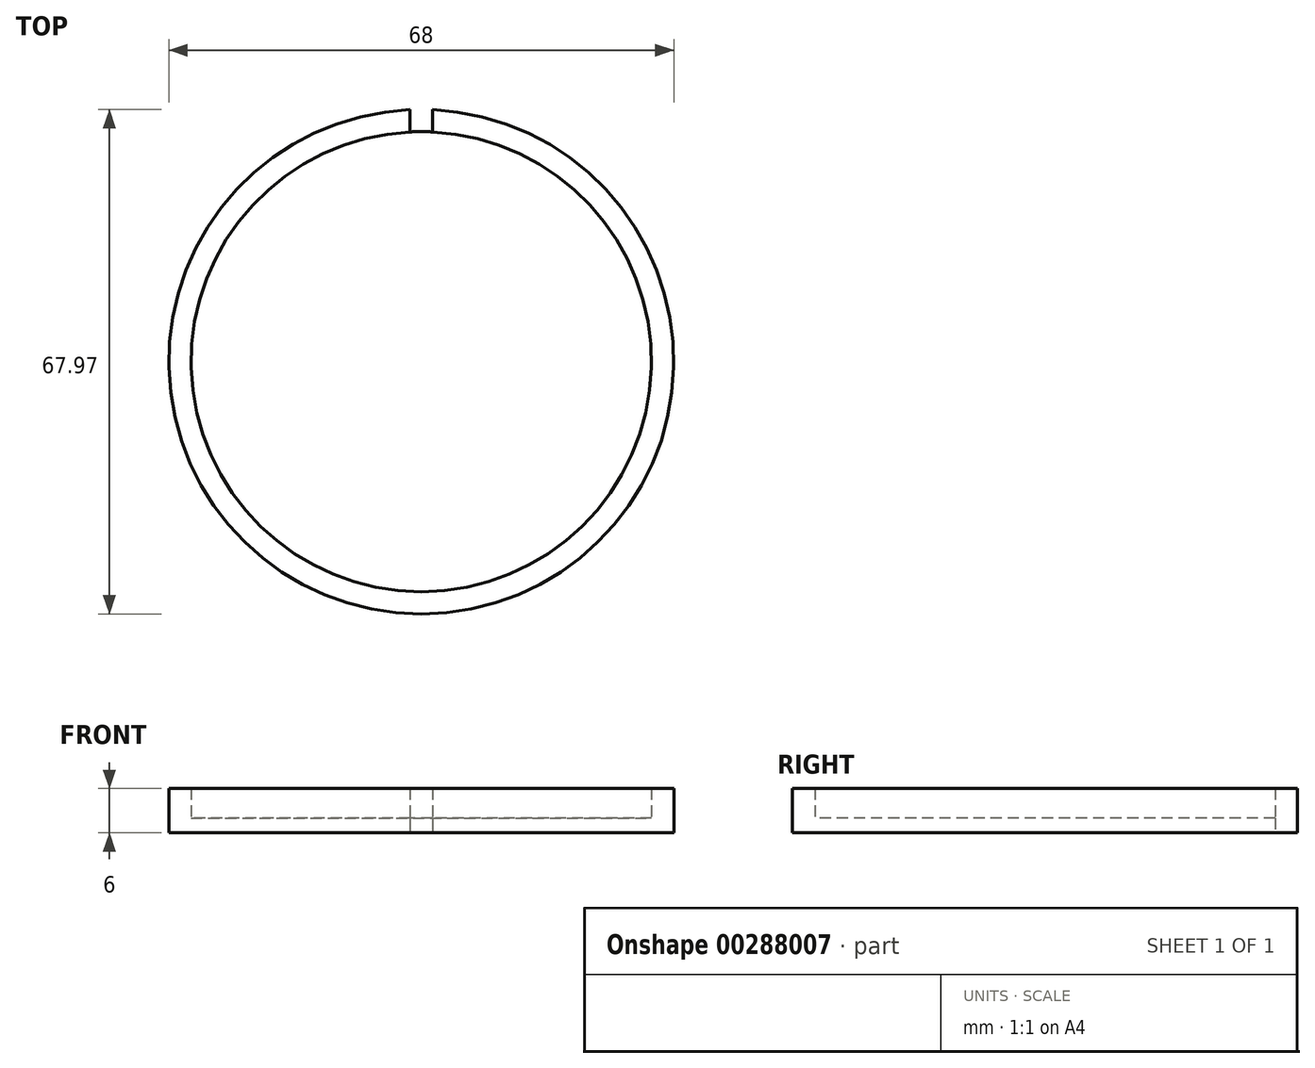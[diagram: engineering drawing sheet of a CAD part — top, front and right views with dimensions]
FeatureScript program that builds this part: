
annotation { "Feature Type Name" : "Feature", "Feature Type Description" : "" }
export const myFeature = defineFeature(function(context is Context, id is Id, definition is map)
    precondition{}
    {
        {
            var Q0;
            Q0=qCreatedBy(makeId("Top.planeOp"),FACE);
            var sketch = newSketch(context, id + "F0", { "sketchPlane" : qUnion([Q0])});
            skCircle(sketch, "E0", {"center": v(0, 0) * mm, "radius": 34 * mm});
            skCircle(sketch, "E1", {"center": v(0, 0) * mm, "radius": 31 * mm});
            skLineSegment(sketch, "E2.bottom", {"start": v(1.5, 25.6) * mm, "end": v(-1.5, 25.6) * mm});
            skLineSegment(sketch, "E2.top", {"start": v(1.5, 36.4) * mm, "end": v(-1.5, 36.4) * mm});
            skLineSegment(sketch, "E2.left", {"start": v(1.5, 25.6) * mm, "end": v(1.5, 36.4) * mm});
            skLineSegment(sketch, "E2.right", {"start": v(-1.5, 25.6) * mm, "end": v(-1.5, 36.4) * mm});
            skPoint(sketch, "E2.middle", {"position": v(0, 31) * mm});
            skSolve(sketch);
        }
        {
            var Q0;
            Q0=makeQuery(id+"F0.imprint","IMPRINT",FACE,{"disambiguationData":[TD([[makeQuery(id+"F0.imprint","IMPRINT",EDGE,{"derivedFrom":sQuery(id+"F0.wireOp",EDGE,"E0")}),1.0]])]});
            extrude(context, id + "F1", {"entities" : qUnion([Q0]), "depth" : 6 * mm});
        }
        {
            var Q0;
            Q0=makeQuery(id+"F0.imprint","IMPRINT",FACE,{"disambiguationData":[TD([[makeQuery(id+"F0.imprint","IMPRINT",EDGE,{"derivedFrom":sQuery(id+"F0.wireOp",EDGE,"E1")}),1.0]])]});
            extrude(context, id + "F2", {"entities" : qUnion([Q0]), "operationType" : NewBodyOperationType.ADD, "depth" : 2 * mm});
        }
        {
            var Q0;
            {var subQ0=sQuery(id+"F0.wireOp",EDGE,"E2.left");var subQ1=sQuery(id+"F0.wireOp",EDGE,"E0");var subQ2=makeQuery(id+"F0.imprint","INTERSECT",VERTEX,{"derivedFrom":[subQ1,subQ0]});Q0=makeQuery(id+"F0.imprint","IMPRINT",FACE,{"disambiguationData":[TD([[makeQuery(id+"F0.imprint","IMPRINT",EDGE,{"disambiguationData":[TD([[subQ2,-1.0]])],"derivedFrom":subQ1}),1.0]])]});}
            extrude(context, id + "F3", {"entities" : qUnion([Q0]), "operationType" : NewBodyOperationType.REMOVE, "depth" : 25 * mm});
        }
    });
